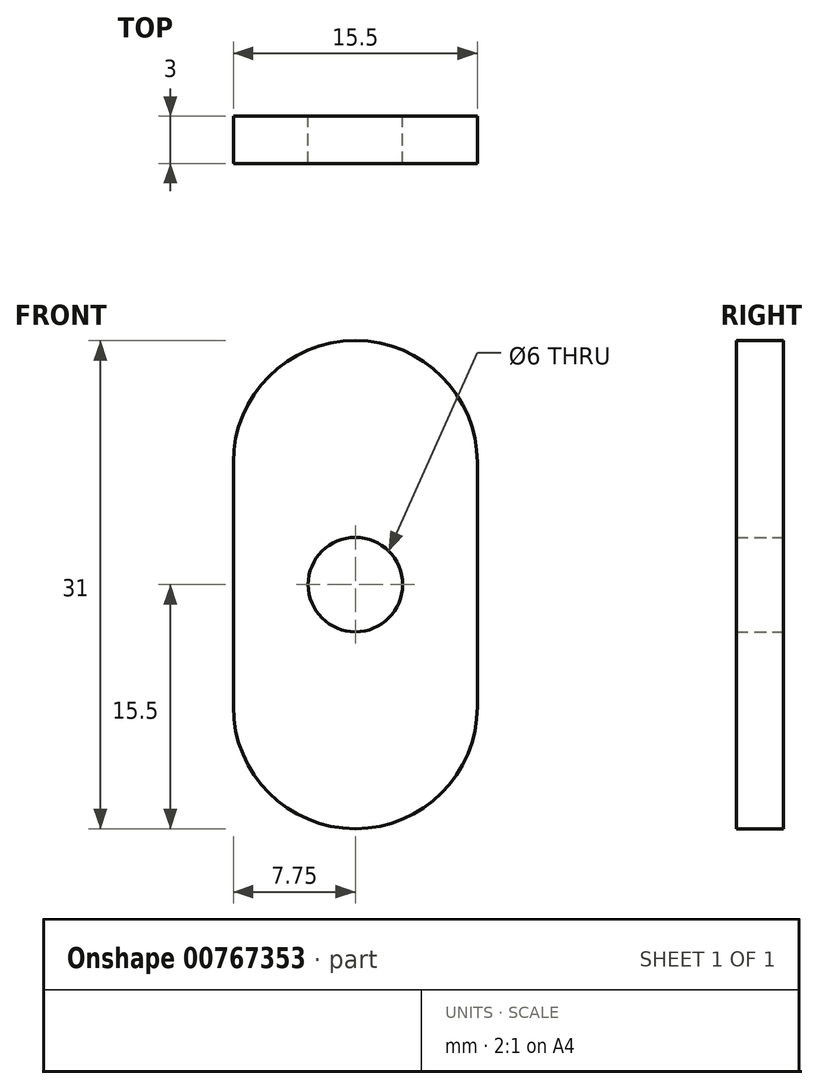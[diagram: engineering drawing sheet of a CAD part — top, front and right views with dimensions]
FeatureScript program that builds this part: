
annotation { "Feature Type Name" : "Feature", "Feature Type Description" : "" }
export const myFeature = defineFeature(function(context is Context, id is Id, definition is map)
    precondition{}
    {
        {
            var Q0;
            Q0=qCreatedBy(makeId("Front.planeOp"),FACE);
            var sketch = newSketch(context, id + "F0", { "sketchPlane" : qUnion([Q0])});
            skLineSegment(sketch, "E0.left", {"start": v(-7.75, 7.75) * mm, "end": v(-7.75, -7.75) * mm});
            skLineSegment(sketch, "E0.right", {"start": v(7.75, 7.75) * mm, "end": v(7.75, -7.75) * mm});
            skPoint(sketch, "E0.middle", {"position": v(0, 0) * mm});
            skArc(sketch, "E1", {"start": v(7.75, 7.75) * mm, "mid": v(0, 15.5) * mm, "end": v(-7.75, 7.75) * mm});
            skArc(sketch, "E2", {"start": v(-7.75, -7.75) * mm, "mid": v(0, -15.5) * mm, "end": v(7.75, -7.75) * mm});
            skCircle(sketch, "E3", {"center": v(0, 0) * mm, "radius": 3 * mm});
            skSolve(sketch);
        }
        {
            var Q0;
            Q0 = qSketchRegion(id + "F0", true);
            extrude(context, id + "F1", {"entities" : qUnion([Q0]), "depth" : 3 * mm, "offsetDistance" : 25 * mm});
        }
    });
